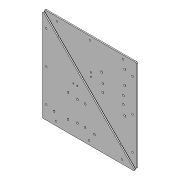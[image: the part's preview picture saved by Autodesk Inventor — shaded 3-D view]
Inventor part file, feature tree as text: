
AUTODESK INVENTOR PART (.ipt)
format: ipt  version: 2020 (Build 240168000, 168)  size: 177,664 bytes
history: native  units: mm
features: other x4, projected_geometry x2, extrude x1, sketch x1
ambient origin geometry x8: Origin, YZ Plane, XZ Plane, XY Plane, X Axis, Y Axis, Z Axis, Center Point
bodies: Body1 (feature_tree)
feature tree (8):
  other  "Display_CCM_Mount.iam"
  other  "Display_CCM_Mount.ipt:1"
  other  "Display_CCM_Mount.ipt:2"
  other  "ソリッド1"
  extrude  "押し出し1"  Depth=10.0mm
  sketch  "スケッチ1"
  projected_geometry  "投影ループ1"
  projected_geometry  "投影ループ2"
